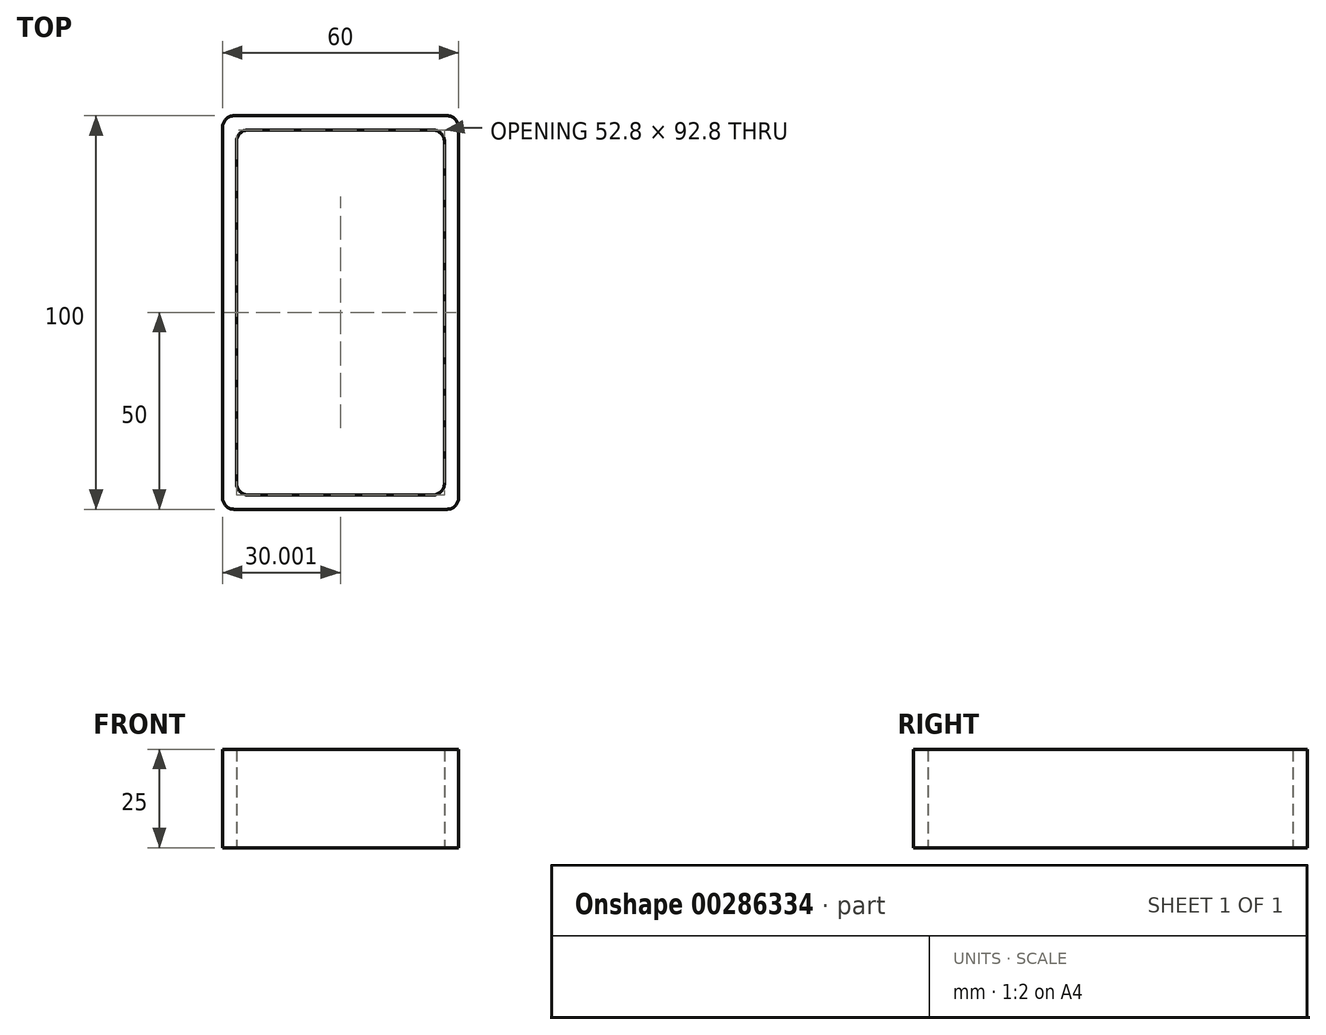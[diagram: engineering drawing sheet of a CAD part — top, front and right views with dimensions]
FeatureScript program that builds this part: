
annotation { "Feature Type Name" : "Feature", "Feature Type Description" : "" }
export const myFeature = defineFeature(function(context is Context, id is Id, definition is map)
    precondition{}
    {
        {
            var Q0;
            Q0=qCreatedBy(makeId("Top.planeOp"),FACE);
            var sketch = newSketch(context, id + "F0", { "sketchPlane" : qUnion([Q0])});
            skLineSegment(sketch, "E0", {"start": v(-45.4, 50) * mm, "end": v(8.6, 50) * mm});
            skLineSegment(sketch, "E1", {"start": v(11.6, 47) * mm, "end": v(11.6, -47) * mm});
            skLineSegment(sketch, "E2", {"start": v(8.6, -50) * mm, "end": v(-45.4, -50) * mm});
            skLineSegment(sketch, "E3", {"start": v(-48.4, -47) * mm, "end": v(-48.4, 47) * mm});
            skLineSegment(sketch, "E4", {"start": v(-18.4, 46.4) * mm, "end": v(-41.8, 46.4) * mm});
            skLineSegment(sketch, "E5", {"start": v(-18.4, 46.4) * mm, "end": v(5, 46.4) * mm});
            skLineSegment(sketch, "E6", {"start": v(-44.8, 23.05) * mm, "end": v(-44.8, 43.4) * mm});
            skLineSegment(sketch, "E7", {"start": v(-44.8, 23.05) * mm, "end": v(-44.8, -43.4) * mm});
            skLineSegment(sketch, "E8", {"start": v(-18.4, -46.4) * mm, "end": v(-41.8, -46.4) * mm});
            skLineSegment(sketch, "E9", {"start": v(-18.4, -46.4) * mm, "end": v(5, -46.4) * mm});
            skLineSegment(sketch, "E10", {"start": v(8, 23.05) * mm, "end": v(8, 43.4) * mm});
            skLineSegment(sketch, "E11", {"start": v(8, 23.05) * mm, "end": v(8, -43.4) * mm});
            skPoint(sketch, "E12.start.orphan", {"position": v(-18.4, -50) * mm});
            skArc(sketch, "E13.filletArc", {"start": v(-45.4, 50) * mm, "mid": v(-47.53, 49.12) * mm, "end": v(-48.4, 47) * mm});
            skArc(sketch, "E14.filletArc", {"start": v(11.6, 47) * mm, "mid": v(10.71, 49.12) * mm, "end": v(8.6, 50) * mm});
            skArc(sketch, "E15.filletArc", {"start": v(-48.4, -47) * mm, "mid": v(-47.53, -49.12) * mm, "end": v(-45.4, -50) * mm});
            skArc(sketch, "E16.filletArc", {"start": v(8.6, -50) * mm, "mid": v(10.71, -49.12) * mm, "end": v(11.6, -47) * mm});
            skArc(sketch, "E17.filletArc", {"start": v(5, -46.4) * mm, "mid": v(7.11, -45.52) * mm, "end": v(8, -43.4) * mm});
            skArc(sketch, "E18.filletArc", {"start": v(8, 43.4) * mm, "mid": v(7.11, 45.52) * mm, "end": v(5, 46.4) * mm});
            skArc(sketch, "E19.filletArc", {"start": v(-41.8, 46.4) * mm, "mid": v(-43.93, 45.52) * mm, "end": v(-44.8, 43.4) * mm});
            skArc(sketch, "E20.filletArc", {"start": v(-44.8, -43.4) * mm, "mid": v(-43.93, -45.52) * mm, "end": v(-41.8, -46.4) * mm});
            skSolve(sketch);
        }
        {
            var Q0;
            Q0 = qSketchRegion(id + "F0", true);
            extrude(context, id + "F1", {"entities" : qUnion([Q0]), "depth" : 25 * mm});
        }
    });
